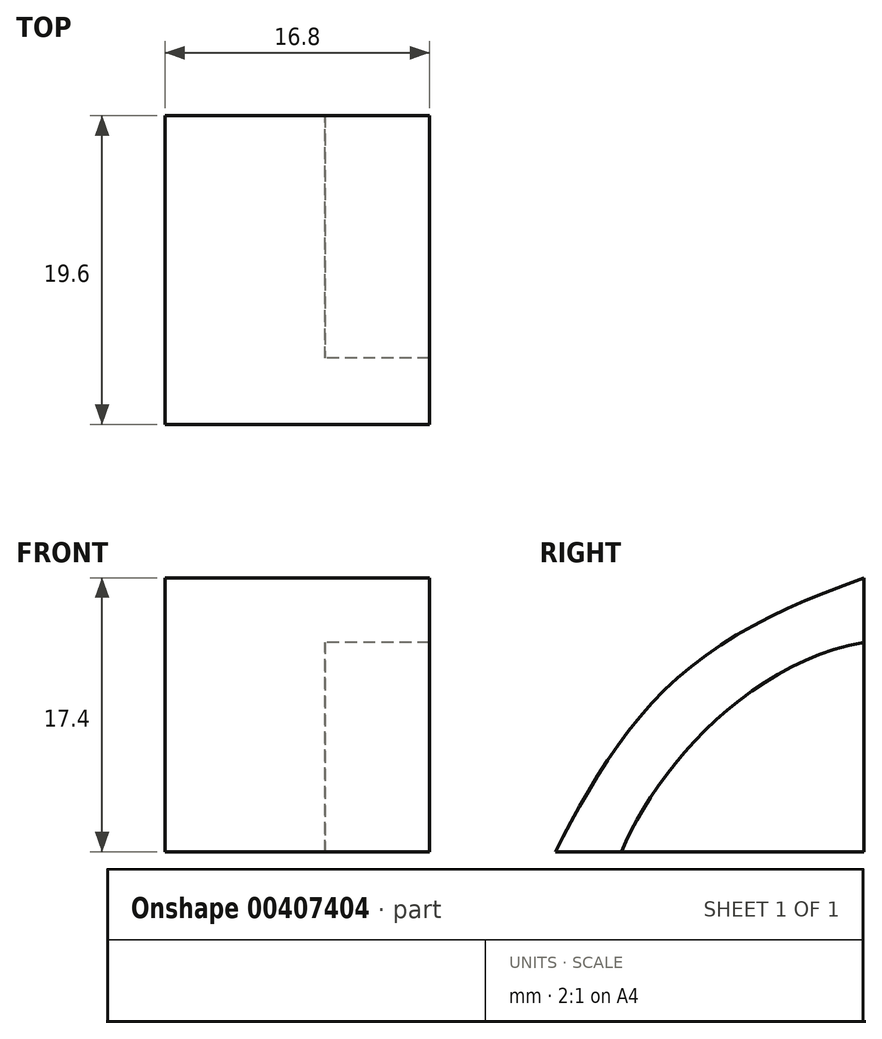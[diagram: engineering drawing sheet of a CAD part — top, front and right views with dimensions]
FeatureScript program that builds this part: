
annotation { "Feature Type Name" : "Feature", "Feature Type Description" : "" }
export const myFeature = defineFeature(function(context is Context, id is Id, definition is map)
    precondition{}
    {
        {
            var Q0;
            Q0=qCreatedBy(makeId("Front.planeOp"),FACE);
            var sketch = newSketch(context, id + "F0", { "sketchPlane" : qUnion([Q0])});
            skCircle(sketch, "E0", {"center": v(0, 0) * mm, "radius": 4.95 * mm});
            skSolve(sketch);
        }
        {
            var Q0;
            Q0=makeQuery(id+"F0.imprint","IMPRINT",FACE,{"disambiguationData":[TD([[makeQuery(id+"F0.imprint","IMPRINT",EDGE,{"derivedFrom":sQuery(id+"F0.wireOp",EDGE,"E0")}),1.0]])]});
            var Q1;
            Q1 = qConstructionFilter(qBodyType(qCreatedBy(id + "F0" ,EDGE), BodyType.WIRE), ConstructionObject.NO);
            extrude(context, id + "F1", {"entities" : qUnion([Q0]), "bodyType" : ToolBodyType.SURFACE, "surfaceEntities" : qUnion([Q1]), "depth" : 28.3 * mm});
        }
        {
            var Q0;
            Q0=qCreatedBy(makeId("Right.planeOp"),FACE);
            var sketch = newSketch(context, id + "F2", { "sketchPlane" : qUnion([Q0])});
            skLineSegment(sketch, "E1", {"start": v(-28.35, 12.46) * mm, "end": v(-28.35, -4.94) * mm});
            skLineSegment(sketch, "E2", {"start": v(-28.35, -4.94) * mm, "end": v(-47.95, -4.94) * mm});
            skFitSpline(sketch, "E3", {"points": [v(-47.95, -4.94) * mm, v(-40.96, 5.39) * mm, v(-28.35, 12.46) * mm], "startDerivative": vector(10.83, 21.46) * mm, "endDerivative": vector(29.86, 10.6) * mm});
            skFitSpline(sketch, "E4", {"points": [v(-43.75, -4.94) * mm, v(-28.35, 8.36) * mm], "startDerivative": vector(5.89, 14.83) * mm, "endDerivative": vector(22.27, 3.77) * mm});
            skSolve(sketch);
        }
        {
            var Q0;
            {var subQ3=sQuery(id+"F2.wireOp",EDGE,"E4");Q0=makeQuery(id+"F2.imprint","IMPRINT",FACE,{"disambiguationData":[TD([[makeQuery(id+"F2.imprint","IMPRINT",EDGE,{"derivedFrom":subQ3}),-1.0]])]});}
            extrude(context, id + "F3", {"entities" : qUnion([Q0]), "endBound" : BoundingType.SYMMETRIC, "depth" : 10.15 * mm});
        }
        {
            var Q0;
            {var subQ0=sQuery(id+"F2.wireOp",EDGE,"E3");Q0=makeQuery(id+"F2.imprint","IMPRINT",FACE,{"disambiguationData":[TD([[makeQuery(id+"F2.imprint","IMPRINT",EDGE,{"derivedFrom":subQ0}),-1.0]])]});}
            extrude(context, id + "F4", {"entities" : qUnion([Q0]), "operationType" : NewBodyOperationType.ADD, "depth" : 11.7 * mm, "hasSecondDirection" : true, "secondDirectionOppositeDirection" : true, "secondDirectionDepth" : 5.1 * mm});
        }
    });
